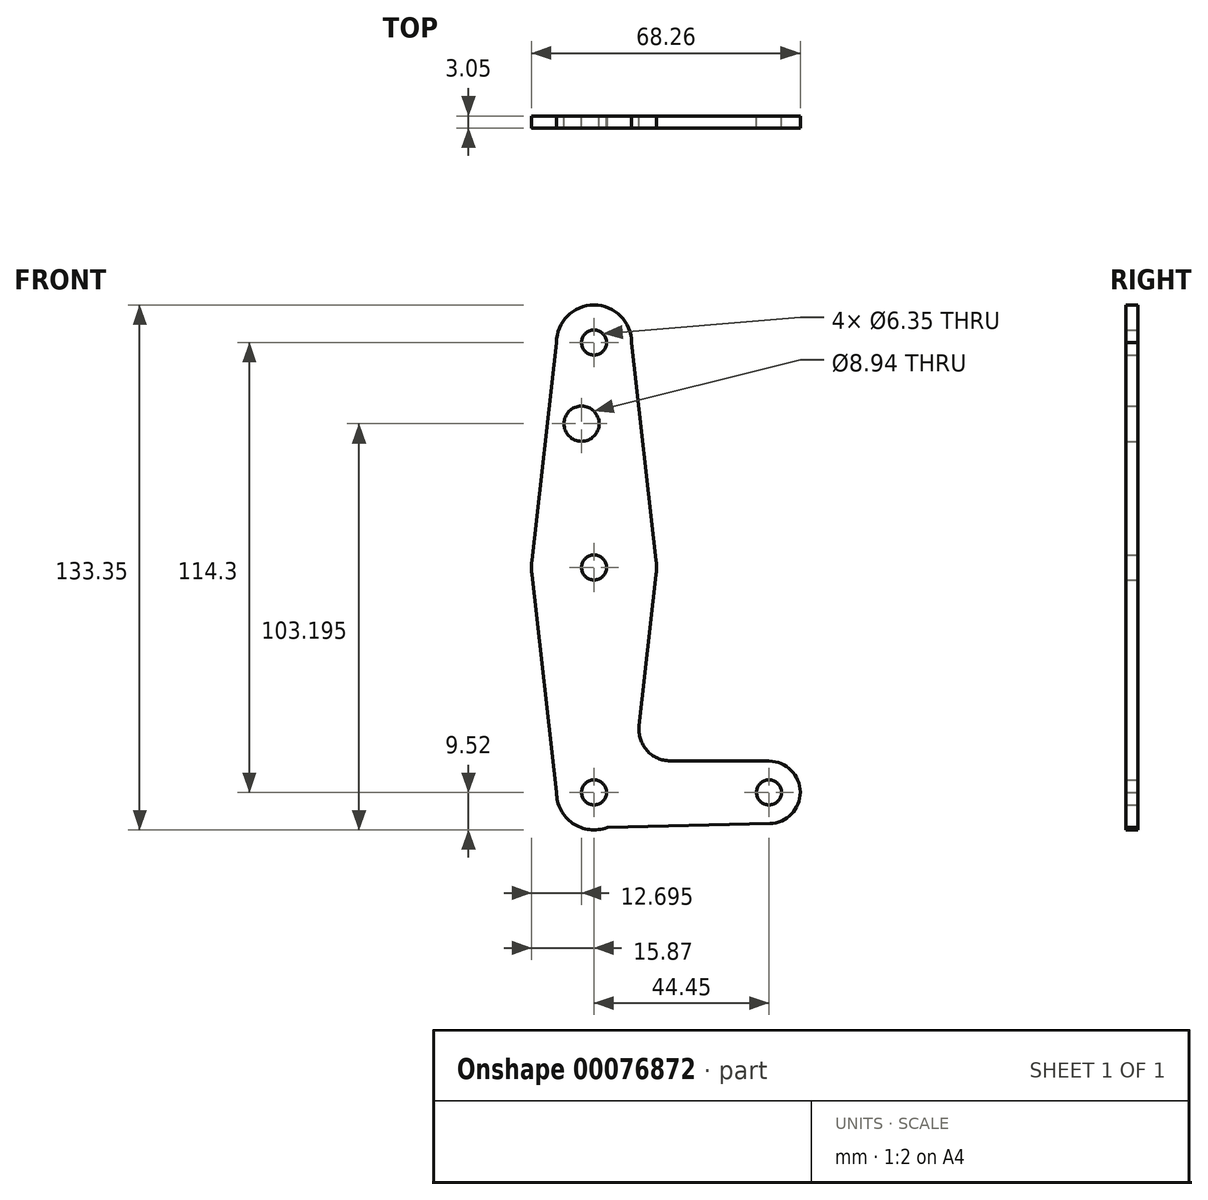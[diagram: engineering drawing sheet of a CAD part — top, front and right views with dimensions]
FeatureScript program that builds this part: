
annotation { "Feature Type Name" : "Feature", "Feature Type Description" : "" }
export const myFeature = defineFeature(function(context is Context, id is Id, definition is map)
    precondition{}
    {
        {
            var Q0;
            Q0=qCreatedBy(makeId("Front.planeOp"),FACE);
            var sketch = newSketch(context, id + "F0", { "sketchPlane" : qUnion([Q0])});
            skLineSegment(sketch, "E0", {"start": v(0, 0) * mm, "end": v(0, 114.3) * mm, "construction": true});
            skCircle(sketch, "E1", {"center": v(0, 114.3) * mm, "radius": 9.53 * mm});
            skCircle(sketch, "E2", {"center": v(0, 57.15) * mm, "radius": 15.88 * mm});
            skCircle(sketch, "E3", {"center": v(0, 0) * mm, "radius": 9.53 * mm});
            skLineSegment(sketch, "E4", {"start": v(0, 0) * mm, "end": v(44.45, 0) * mm, "construction": true});
            skCircle(sketch, "E5", {"center": v(44.45, 0) * mm, "radius": 7.94 * mm});
            skLineSegment(sketch, "E6", {"start": v(9.53, 114.3) * mm, "end": v(15.77, 58.93) * mm});
            skLineSegment(sketch, "E7", {"start": v(-9.53, 114.3) * mm, "end": v(-15.77, 58.93) * mm});
            skLineSegment(sketch, "E8", {"start": v(-15.77, 55.37) * mm, "end": v(-9.52, 0) * mm});
            skLineSegment(sketch, "E9", {"start": v(15.77, 55.37) * mm, "end": v(11.47, 16.85) * mm});
            skLineSegment(sketch, "E10", {"start": v(3.38, -8.9) * mm, "end": v(44.64, -7.94) * mm});
            skLineSegment(sketch, "E11", {"start": v(19.34, 8.02) * mm, "end": v(44.48, 7.94) * mm});
            skCircle(sketch, "E12", {"center": v(0, 114.3) * mm, "radius": 3.18 * mm});
            skCircle(sketch, "E13", {"center": v(0, 57.15) * mm, "radius": 3.18 * mm});
            skCircle(sketch, "E14", {"center": v(0, 0) * mm, "radius": 3.18 * mm});
            skCircle(sketch, "E15", {"center": v(44.45, 0) * mm, "radius": 3.18 * mm});
            skPoint(sketch, "E16.newPointA", {"position": v(9.58, 0) * mm});
            skArc(sketch, "E16.filletArc", {"start": v(11.47, 16.85) * mm, "mid": v(13.44, 10.68) * mm, "end": v(19.34, 8.02) * mm});
            skCircle(sketch, "E17", {"center": v(-3.18, 93.68) * mm, "radius": 4.47 * mm});
            skSolve(sketch);
        }
        {
            var Q0;
            Q0=makeQuery(id+"F0.imprint","IMPRINT",FACE,{"disambiguationData":[TD([[makeQuery(id+"F0.imprint","IMPRINT",EDGE,{"derivedFrom":sQuery(id+"F0.wireOp",EDGE,"E12")}),-1.0]])]});
            var Q1;
            {var subQ0=sQuery(id+"F0.wireOp",EDGE,"E6");Q1=makeQuery(id+"F0.imprint","IMPRINT",FACE,{"disambiguationData":[TD([[makeQuery(id+"F0.imprint","IMPRINT",EDGE,{"derivedFrom":subQ0}),-1.0]])]});}
            var Q2;
            Q2=makeQuery(id+"F0.imprint","IMPRINT",FACE,{"disambiguationData":[TD([[makeQuery(id+"F0.imprint","IMPRINT",EDGE,{"derivedFrom":sQuery(id+"F0.wireOp",EDGE,"E13")}),-1.0]])]});
            var Q3;
            {var subQ0=sQuery(id+"F0.wireOp",EDGE,"E8");Q3=makeQuery(id+"F0.imprint","IMPRINT",FACE,{"disambiguationData":[TD([[makeQuery(id+"F0.imprint","IMPRINT",EDGE,{"derivedFrom":subQ0}),1.0]])]});}
            var Q4;
            Q4=makeQuery(id+"F0.imprint","IMPRINT",FACE,{"disambiguationData":[TD([[makeQuery(id+"F0.imprint","IMPRINT",EDGE,{"derivedFrom":sQuery(id+"F0.wireOp",EDGE,"E14")}),-1.0]])]});
            var Q5;
            Q5=makeQuery(id+"F0.imprint","IMPRINT",FACE,{"disambiguationData":[TD([[makeQuery(id+"F0.imprint","IMPRINT",EDGE,{"derivedFrom":sQuery(id+"F0.wireOp",EDGE,"E15")}),-1.0]])]});
            extrude(context, id + "F1", {"entities" : qUnion([Q0, Q1, Q2, Q3, Q4, Q5]), "depth" : 3.05 * mm});
        }
    });
